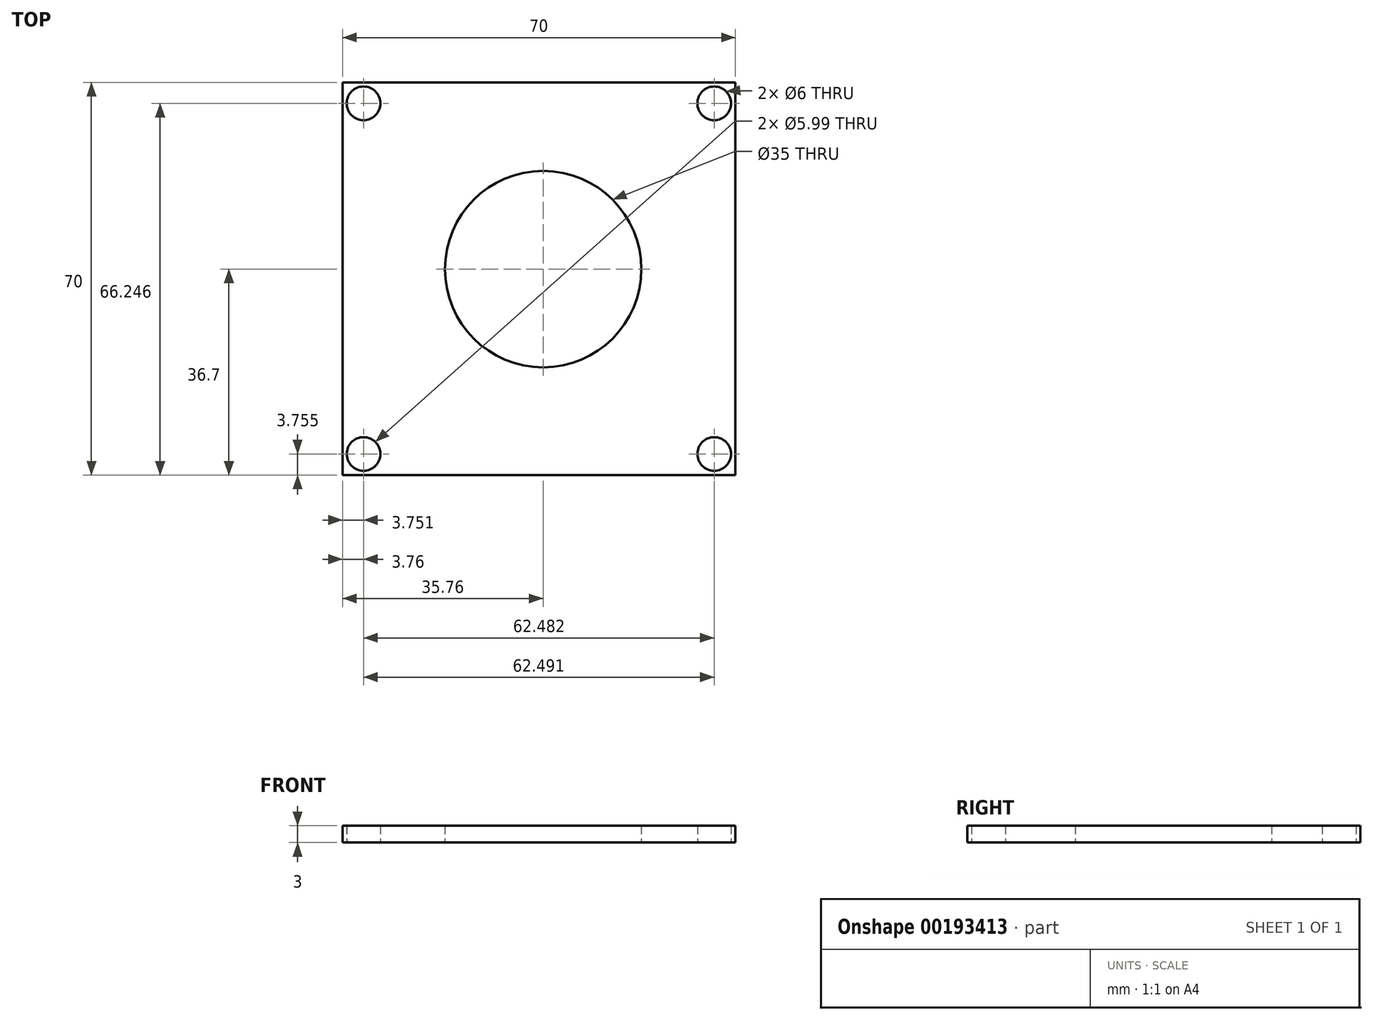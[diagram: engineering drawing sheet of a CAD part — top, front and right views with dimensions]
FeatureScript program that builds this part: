
annotation { "Feature Type Name" : "Feature", "Feature Type Description" : "" }
export const myFeature = defineFeature(function(context is Context, id is Id, definition is map)
    precondition{}
    {
        {
            var Q0;
            Q0=qCreatedBy(makeId("Top.planeOp"),FACE);
            var sketch = newSketch(context, id + "F0", { "sketchPlane" : qUnion([Q0])});
            skLineSegment(sketch, "E0.bottom", {"start": v(-35.76, 33.3) * mm, "end": v(34.24, 33.3) * mm});
            skLineSegment(sketch, "E0.top", {"start": v(-35.76, -36.7) * mm, "end": v(34.24, -36.7) * mm});
            skLineSegment(sketch, "E0.left", {"start": v(-35.76, 33.3) * mm, "end": v(-35.76, -36.7) * mm});
            skLineSegment(sketch, "E0.right", {"start": v(34.24, 33.3) * mm, "end": v(34.24, -36.7) * mm});
            skCircle(sketch, "E1", {"center": v(0, 0) * mm, "radius": 17.5 * mm});
            skCircle(sketch, "E2", {"center": v(-32, 29.55) * mm, "radius": 3 * mm});
            skCircle(sketch, "E3", {"center": v(30.48, 29.55) * mm, "radius": 3 * mm});
            skCircle(sketch, "E4", {"center": v(-32, -32.95) * mm, "radius": 3 * mm});
            skCircle(sketch, "E5", {"center": v(30.48, -32.95) * mm, "radius": 3 * mm});
            skSolve(sketch);
        }
        {
            var Q0;
            Q0 = qSketchRegion(id + "F0", true);
            extrude(context, id + "F1", {"entities" : qUnion([Q0]), "depth" : 3 * mm});
        }
    });
